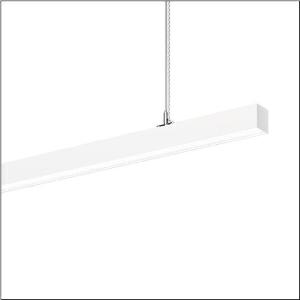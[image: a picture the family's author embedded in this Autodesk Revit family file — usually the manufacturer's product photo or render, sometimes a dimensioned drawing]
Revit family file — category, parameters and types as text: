
# Revit family: silica_r__21_51mx33da47wb_07b3
name_source: partatom
category: Lighting Fixtures
units: mm (PartAtom-declared; Revit-internal decimal feet)

## family parameters
Cut with Voids When Loaded = No
Host = Face
Light Source = No
Part Type = Normal
Room Calculation Point = No
Round Connector Dimension = Use Diameter
Shared = No

## types (1)
- --- (1 x LED, 5910 lm, 38.4 W, 4000K)
    Apparent Load = 38 VA
    CIE Flux Codes = 78 96 99 55 100
    Color Rendering = 80
    Color Temperature = 4000K
    Default Elevation = 1800 mm
    Description = Silica® 21, office luminaire, primary optical cover: prismatic diffuser, of PMMA, CAT 2 (L<= 3000cd/m²), light emission: direct/indirect distribution, primary light characteristic: symmetric, installation type: suspended mounting, LED, rated luminous flux: 5.910lm, luminous efficacy: 154lm/W, light colour: 840, colour temperature: 4000K, with terminal, 3+2-pole, max. 2.5mm², mains connection: 220..240V, AC, 50/60Hz, rated input power: 38.4W, luminaire housing, of aluminium, traffic white (RAL 9016), length: 1.204mm, width: 53mm, height: 53mm, protection rating (complete): IP20, insulation class (complete): insulation class I (protective earthing), certification: CE, permissible operating ambient temperature: 0..+35°C, standard: EN 50419, packaging unit: 1 piece
    Height = 53 mm
    Lamp = 1 x LED
    Lamp Light Flux = 5910 lm
    Lamp Power = 38.4 W
    Lamp count = 1
    Length = 1204 mm
    Luminous efficacy = 154 lm/W
    Manufacturer = Siteco
    ModVariant = No
    Model = 51MX33DA47WB
    Mounting Place = Ceiling
    Mounting Type = Pendant
    Number of Poles = 1
    OnlyDefault = Yes
    Power Factor = 1
    Product Name = Silica® 21
    Product group = office luminaire | ceiling pendant
    ProductGroupID = 902
    Protection Class = Protection class I
    Protection Degree = IP 20
    RLX_Detail_Level = 1
    RLX_Emergency_Light_Flux = 0 lm
    RLX_Emergency_Type = 0
    RLX_Emergency_Type_DB = No
    RlxData = <blob elided: 21157 chars, md5=76965f25>
    Socket = socket
    Standby Power = 0 W
    System Light Flux = 5910 lm
    System Power = 38 W
    Type Comments = factory setting: luminous flux: 100 % | dim-lin: 254 | 323 mA
    Type Image = l_1313629.jpg
    URL = http://relux.com
    VarID = @adj_067437
    Voltage = 0 V
    Weight = 0.00 kg
    Width = 53 mm

## geometry (parser evidence)
native form markers: Blend x4, Sweep x12
no freeform markers — native parametric forms only
